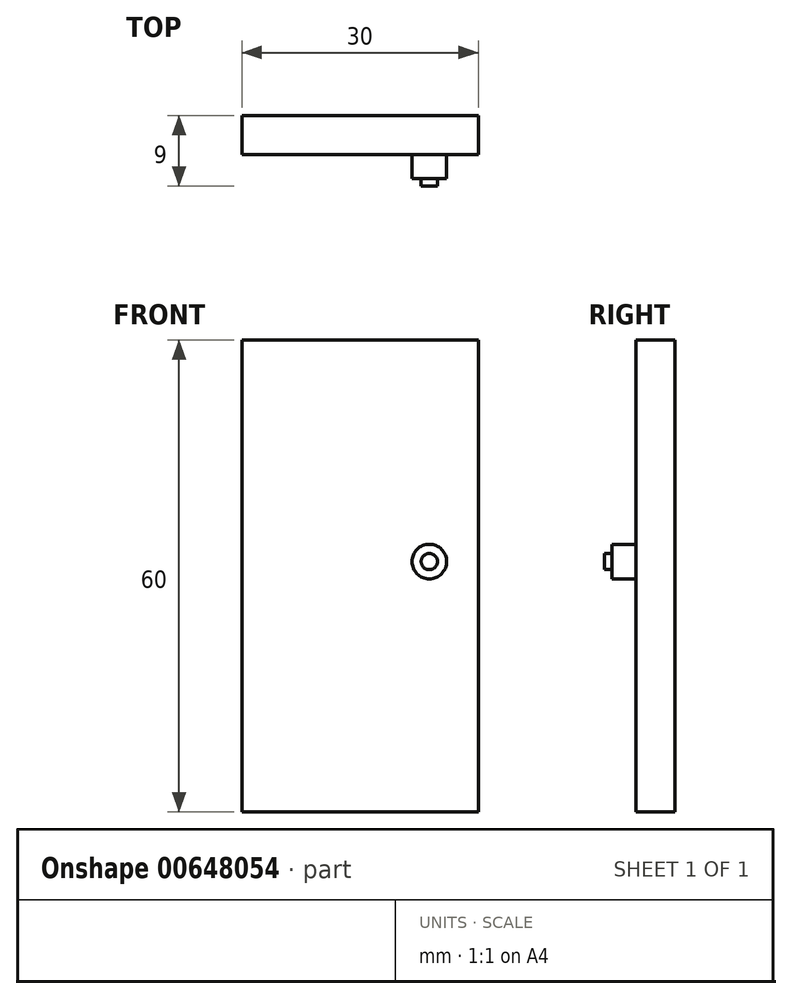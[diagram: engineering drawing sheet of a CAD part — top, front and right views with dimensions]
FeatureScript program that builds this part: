
annotation { "Feature Type Name" : "Feature", "Feature Type Description" : "" }
export const myFeature = defineFeature(function(context is Context, id is Id, definition is map)
    precondition{}
    {
        {
            var Q0;
            Q0=qCreatedBy(makeId("Front.planeOp"),FACE);
            var sketch = newSketch(context, id + "F0", { "sketchPlane" : qUnion([Q0])});
            skLineSegment(sketch, "E0.bottom", {"start": v(-31.13, 7.08) * mm, "end": v(-1.13, 7.08) * mm});
            skLineSegment(sketch, "E0.top", {"start": v(-31.13, -52.92) * mm, "end": v(-1.13, -52.92) * mm});
            skLineSegment(sketch, "E0.left", {"start": v(-31.13, 7.08) * mm, "end": v(-31.13, -52.92) * mm});
            skLineSegment(sketch, "E0.right", {"start": v(-1.13, 7.08) * mm, "end": v(-1.13, -52.92) * mm});
            skSolve(sketch);
        }
        {
            var Q0;
            Q0=makeQuery(id+"F0.imprint","IMPRINT",FACE,{"disambiguationData":[TD([[makeQuery(id+"F0.imprint","IMPRINT",EDGE,{"derivedFrom":sQuery(id+"F0.wireOp",EDGE,"E0.bottom")}),-1.0]])]});
            extrude(context, id + "F1", {"entities" : qUnion([Q0]), "depth" : 5 * mm, "offsetDistance" : 25 * mm});
        }
        {
            var Q0;
            Q0=makeQuery(id+"F1.opExtrude","CAP_FACE",FACE,{"disambiguationData":[OSD([sQuery(id+"F0.wireOp",EDGE,"E0.bottom"),sQuery(id+"F0.wireOp",EDGE,"E0.top"),sQuery(id+"F0.wireOp",EDGE,"E0.left"),sQuery(id+"F0.wireOp",EDGE,"E0.right")])],"isStart":false});
            var sketch = newSketch(context, id + "F2", { "sketchPlane" : qUnion([Q0])});
            skCircle(sketch, "E1", {"center": v(-7.35, -21.1) * mm, "radius": 2.2 * mm});
            skSolve(sketch);
        }
        {
            var Q0;
            Q0=makeQuery(id+"F2.imprint","IMPRINT",FACE,{"disambiguationData":[TD([[makeQuery(id+"F2.imprint","IMPRINT",EDGE,{"derivedFrom":sQuery(id+"F2.wireOp",EDGE,"E1")}),1.0]])]});
            extrude(context, id + "F3", {"entities" : qUnion([Q0]), "operationType" : NewBodyOperationType.ADD, "depth" : 3 * mm, "offsetDistance" : 25 * mm});
        }
        {
            var Q0;
            Q0=makeQuery(id+"F3.opExtrude","CAP_FACE",FACE,{"disambiguationData":[OSD([sQuery(id+"F2.wireOp",EDGE,"E1")])],"isStart":false});
            var sketch = newSketch(context, id + "F4", { "sketchPlane" : qUnion([Q0])});
            skCircle(sketch, "E2", {"center": v(-7.35, -21.1) * mm, "radius": 1.03 * mm});
            skSolve(sketch);
        }
        {
            var Q0;
            Q0 = qSketchRegion(id + "F4", true);
            extrude(context, id + "F5", {"entities" : qUnion([Q0]), "operationType" : NewBodyOperationType.ADD, "depth" : 1 * mm, "offsetDistance" : 25 * mm});
        }
    });
